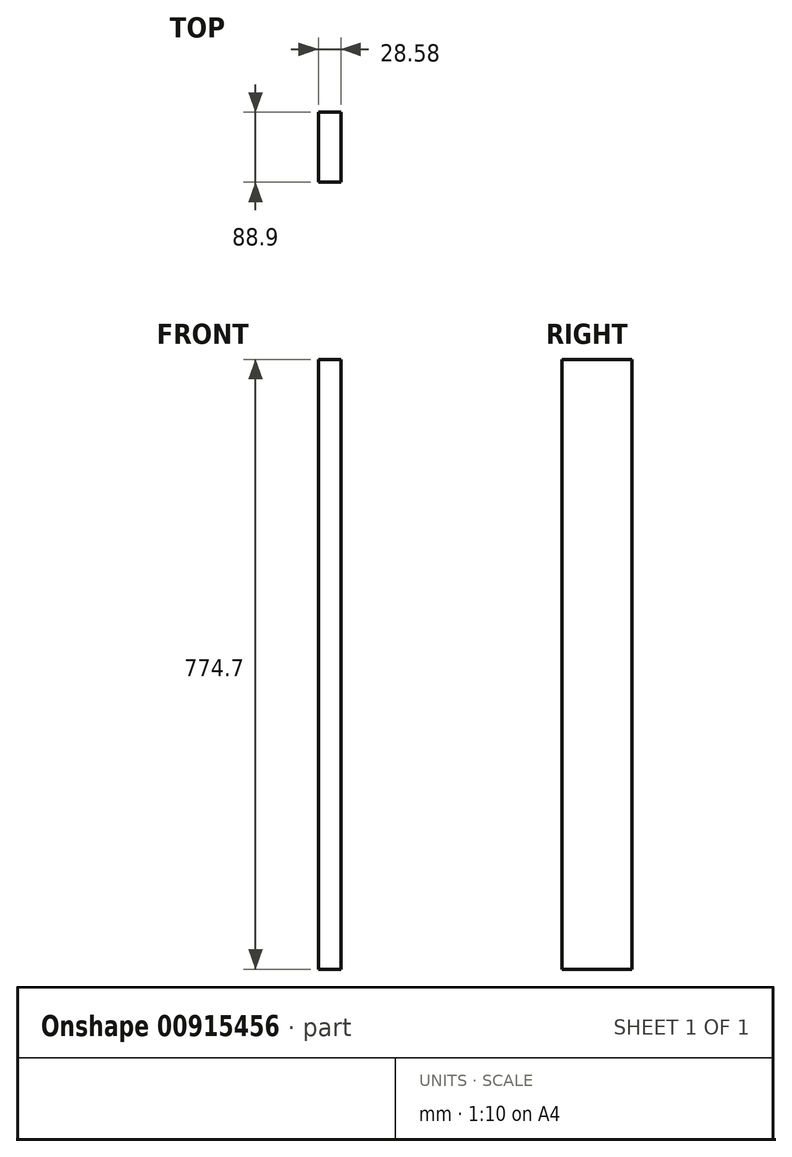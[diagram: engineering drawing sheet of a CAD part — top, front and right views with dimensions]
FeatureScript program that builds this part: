
annotation { "Feature Type Name" : "Feature", "Feature Type Description" : "" }
export const myFeature = defineFeature(function(context is Context, id is Id, definition is map)
    precondition{}
    {
        {
            var Q0;
            Q0=qCreatedBy(makeId("Top.planeOp"),FACE);
            var sketch = newSketch(context, id + "F0", { "sketchPlane" : qUnion([Q0])});
            skLineSegment(sketch, "E0.bottom", {"start": v(14.29, 44.45) * mm, "end": v(-14.29, 44.45) * mm});
            skLineSegment(sketch, "E0.top", {"start": v(14.29, -44.45) * mm, "end": v(-14.29, -44.45) * mm});
            skLineSegment(sketch, "E0.left", {"start": v(14.29, 44.45) * mm, "end": v(14.29, -44.45) * mm});
            skLineSegment(sketch, "E0.right", {"start": v(-14.29, 44.45) * mm, "end": v(-14.29, -44.45) * mm});
            skPoint(sketch, "E0.middle", {"position": v(0, 0) * mm});
            skSolve(sketch);
        }
        {
            var Q0;
            Q0=makeQuery(id+"F0.imprint","IMPRINT",FACE,{"disambiguationData":[TD([[makeQuery(id+"F0.imprint","IMPRINT",EDGE,{"derivedFrom":sQuery(id+"F0.wireOp",EDGE,"E0.bottom")}),1.0]])]});
            extrude(context, id + "F1", {"entities" : qUnion([Q0]), "depth" : 774.7 * mm, "offsetDistance" : 25.4 * mm});
        }
    });
